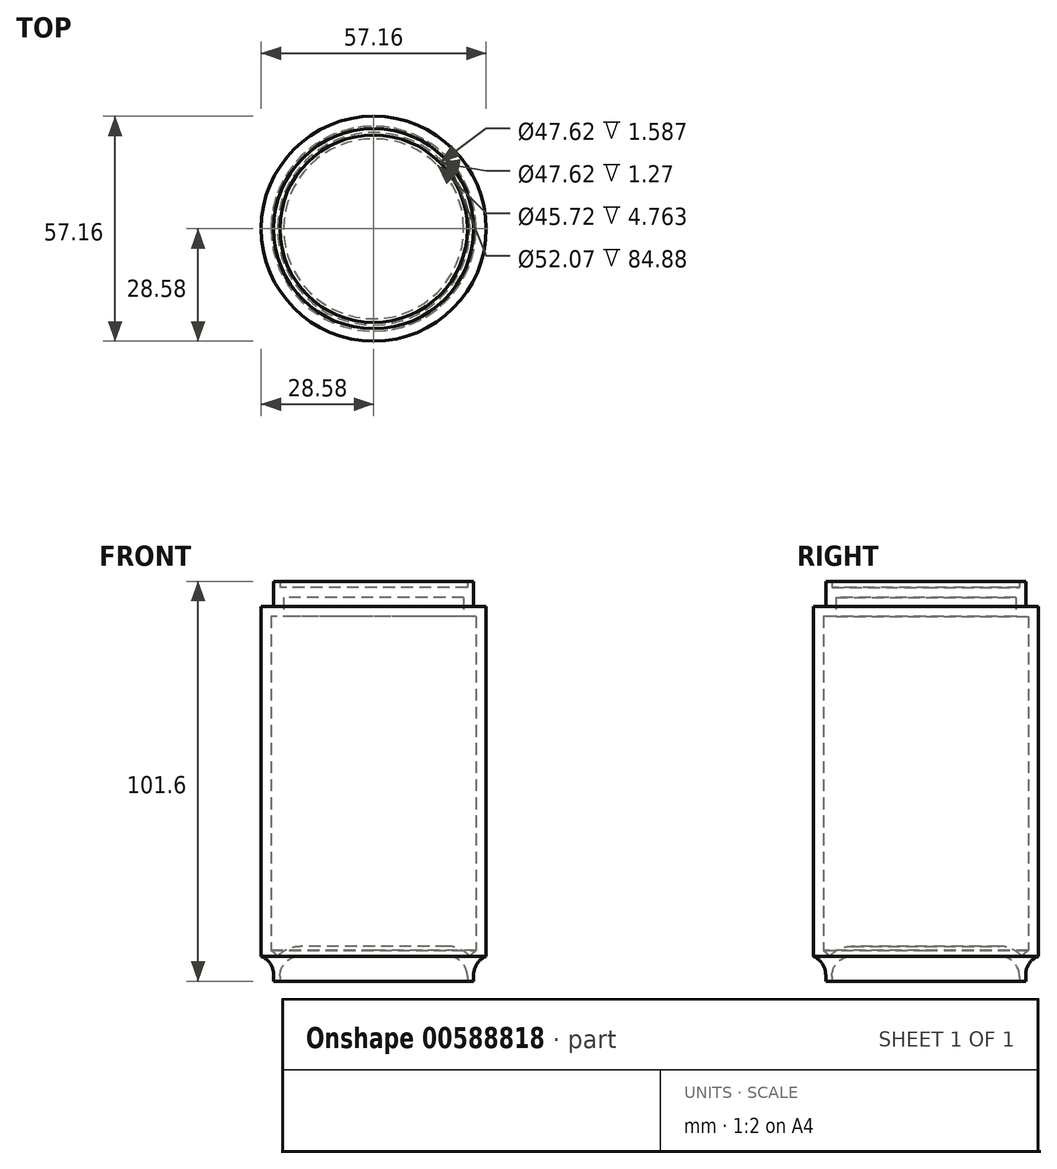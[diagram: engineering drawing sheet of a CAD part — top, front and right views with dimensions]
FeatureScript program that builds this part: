
annotation { "Feature Type Name" : "Feature", "Feature Type Description" : "" }
export const myFeature = defineFeature(function(context is Context, id is Id, definition is map)
    precondition{}
    {
        {
            var Q0;
            Q0=qCreatedBy(makeId("Top.planeOp"),FACE);
            var sketch = newSketch(context, id + "F0", { "sketchPlane" : qUnion([Q0])});
            skCircle(sketch, "E0", {"center": v(0, 0) * mm, "radius": 25.4 * mm});
            skCircle(sketch, "E1", {"center": v(0, 0) * mm, "radius": 28.58 * mm});
            skCircle(sketch, "E2", {"center": v(0, 0) * mm, "radius": 23.81 * mm});
            skSolve(sketch);
        }
        {
            var Q0;
            Q0=makeQuery(id+"F0.imprint","IMPRINT",FACE,{"disambiguationData":[TD([[makeQuery(id+"F0.imprint","IMPRINT",EDGE,{"derivedFrom":sQuery(id+"F0.wireOp",EDGE,"E0")}),-1.0]])]});
            extrude(context, id + "F1", {"entities" : qUnion([Q0]), "depth" : 95.25 * mm, "offsetDistance" : 25.4 * mm});
        }
        {
            var Q0;
            Q0=makeQuery(id+"F0.imprint","IMPRINT",FACE,{"disambiguationData":[TD([[makeQuery(id+"F0.imprint","IMPRINT",EDGE,{"derivedFrom":sQuery(id+"F0.wireOp",EDGE,"E0")}),1.0]])]});
            extrude(context, id + "F2", {"entities" : qUnion([Q0]), "operationType" : NewBodyOperationType.ADD, "depth" : 101.6 * mm, "offsetDistance" : 25.4 * mm});
        }
        {
            var Q0;
            Q0=makeQuery(id+"F0.imprint","IMPRINT",FACE,{"disambiguationData":[TD([[makeQuery(id+"F0.imprint","IMPRINT",EDGE,{"derivedFrom":sQuery(id+"F0.wireOp",EDGE,"E0")}),-1.0]])]});
            extrude(context, id + "F3", {"entities" : qUnion([Q0]), "operationType" : NewBodyOperationType.REMOVE, "depth" : 6.35 * mm, "offsetDistance" : 25.4 * mm});
        }
        {
            var Q0;
            Q0=makeQuery(id+"F0.imprint","IMPRINT",FACE,{"disambiguationData":[TD([[makeQuery(id+"F0.imprint","IMPRINT",EDGE,{"derivedFrom":sQuery(id+"F0.wireOp",EDGE,"E2")}),1.0]])]});
            extrude(context, id + "F4", {"entities" : qUnion([Q0]), "operationType" : NewBodyOperationType.ADD, "depth" : 100.01 * mm, "offsetDistance" : 25.4 * mm});
        }
        {
            var Q0;
            Q0=makeQuery(id+"F0.imprint","IMPRINT",FACE,{"disambiguationData":[TD([[makeQuery(id+"F0.imprint","IMPRINT",EDGE,{"derivedFrom":sQuery(id+"F0.wireOp",EDGE,"E2")}),1.0]])]});
            extrude(context, id + "F5", {"entities" : qUnion([Q0]), "operationType" : NewBodyOperationType.ADD, "depth" : 6.35 * mm, "offsetDistance" : 25.4 * mm});
        }
        {
            var Q0;
            Q0=makeQuery(id+"F0.imprint","IMPRINT",FACE,{"disambiguationData":[TD([[makeQuery(id+"F0.imprint","IMPRINT",EDGE,{"derivedFrom":sQuery(id+"F0.wireOp",EDGE,"E2")}),1.0]])]});
            extrude(context, id + "F6", {"entities" : qUnion([Q0]), "operationType" : NewBodyOperationType.REMOVE, "depth" : 6.35 * mm, "offsetDistance" : 25.4 * mm});
        }
        {
            var Q0;
            Q0=makeQuery(id+"F6.boolean.opBoolean","COPY",EDGE,{"derivedFrom":makeQuery(id+"F6.opExtrude","CAP_EDGE",EDGE,{"disambiguationData":[OSD([sQuery(id+"F0.wireOp",EDGE,"E2")])],"isStart":false})});
            fillet(context, id + "F7", {"entities" : qUnion([Q0]), "radius" : 5.08 * mm, "tangentPropagation" : true, "allowEdgeOverflow" : false});
        }
        {
            var Q0;
            Q0=makeQuery(id+"F3.boolean.opBoolean","COPY",EDGE,{"derivedFrom":makeQuery(id+"F3.opExtrude","CAP_EDGE",EDGE,{"disambiguationData":[OSD([sQuery(id+"F0.wireOp",EDGE,"E0")])],"isStart":false})});
            var Q1;
            Q1=makeQuery(id+"F1.opExtrude","CAP_EDGE",EDGE,{"disambiguationData":[OSD([sQuery(id+"F0.wireOp",EDGE,"E0")])],"isStart":false});
            fillet(context, id + "F8", {"entities" : qUnion([Q0, Q1]), "radius" : 5.08 * mm, "tangentPropagation" : true, "allowEdgeOverflow" : false});
        }
        {
            var Q0;
            Q0=makeQuery(id+"F1.opExtrude","SWEPT_FACE",FACE,{"disambiguationData":[OSD([sQuery(id+"F0.wireOp",EDGE,"E1")])]});
            var Q1;
            Q1=makeQuery(id+"F1.opExtrude","SWEPT_BODY",BODY,{"disambiguationData":[OSD([sQuery(id+"F0.wireOp",EDGE,"E0"),sQuery(id+"F0.wireOp",EDGE,"E1")])]});
            shell(context, id + "F9", {"isHollow" : true, "entities" : qUnion([Q0]), "parts" : qUnion([Q1]), "thickness" : 2.54 * mm});
        }
    });
